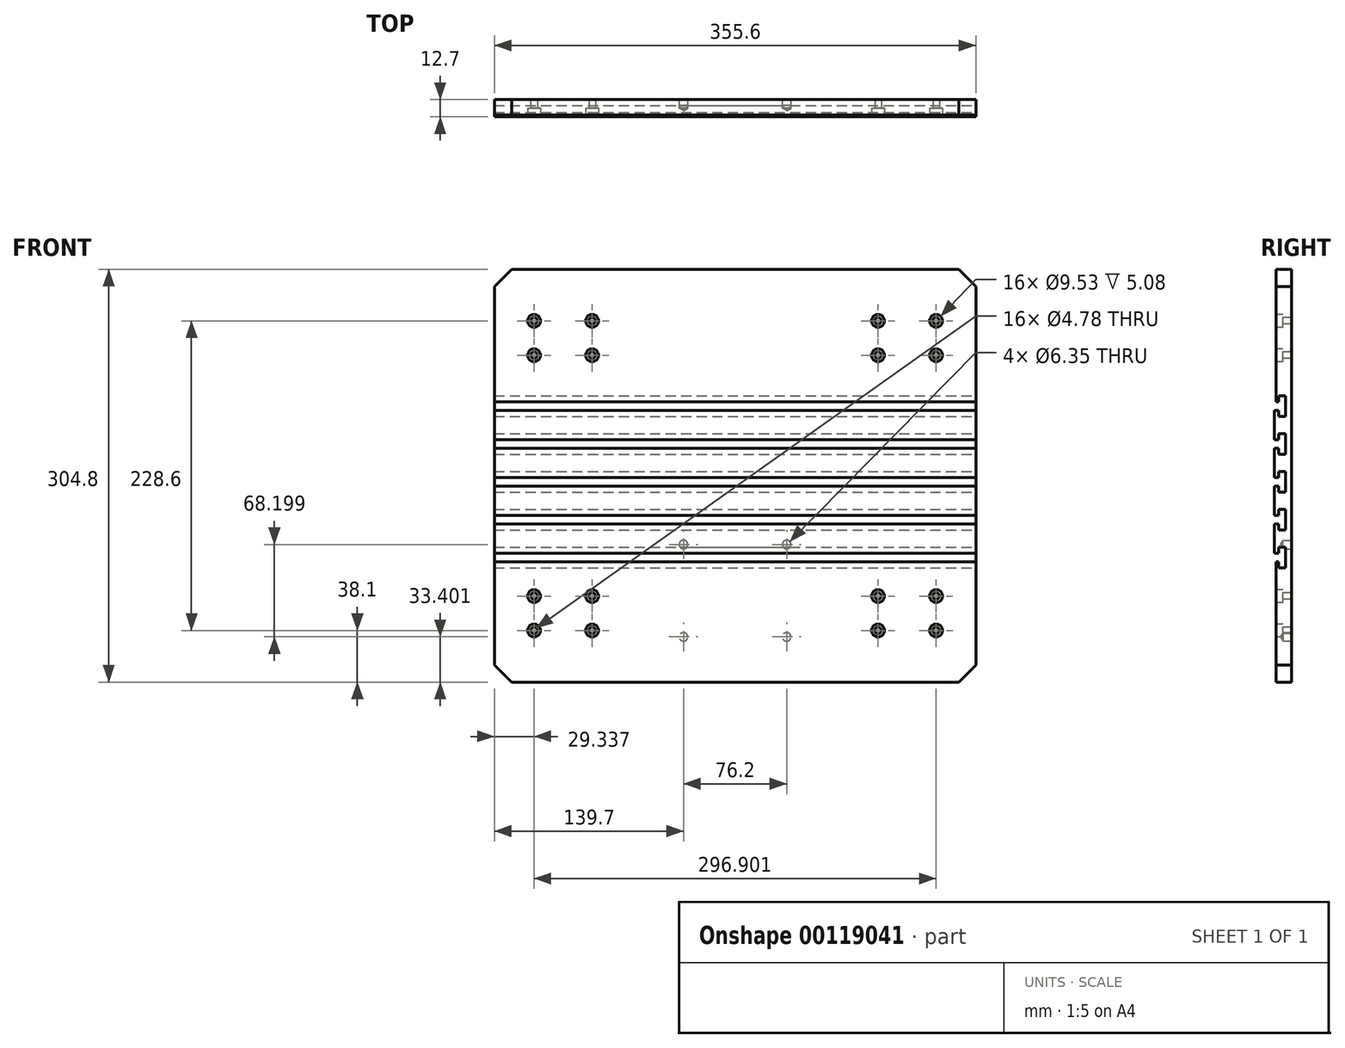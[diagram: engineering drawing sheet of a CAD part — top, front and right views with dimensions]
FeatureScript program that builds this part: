
annotation { "Feature Type Name" : "Feature", "Feature Type Description" : "" }
export const myFeature = defineFeature(function(context is Context, id is Id, definition is map)
    precondition{}
    {
        {
            var Q0;
            Q0=qCreatedBy(makeId("Front.planeOp"),FACE);
            var sketch = newSketch(context, id + "F0", { "sketchPlane" : qUnion([Q0])});
            skLineSegment(sketch, "E0.bottom", {"start": v(0, 0) * mm, "end": v(355.6, 0) * mm});
            skLineSegment(sketch, "E0.top", {"start": v(0, 304.8) * mm, "end": v(355.6, 304.8) * mm});
            skLineSegment(sketch, "E0.left", {"start": v(0, 0) * mm, "end": v(0, 304.8) * mm});
            skLineSegment(sketch, "E0.right", {"start": v(355.6, 0) * mm, "end": v(355.6, 304.8) * mm});
            skSolve(sketch);
        }
        {
            var Q0;
            Q0 = qSketchRegion(id + "F0", true);
            extrude(context, id + "F1", {"entities" : qUnion([Q0]), "depth" : 12.7 * mm});
        }
        {
            var Q0;
            Q0=makeQuery(id+"F1.opExtrude","CAP_FACE",FACE,{"disambiguationData":[OSD([sQuery(id+"F0.wireOp",EDGE,"E0.bottom"),sQuery(id+"F0.wireOp",EDGE,"E0.top"),sQuery(id+"F0.wireOp",EDGE,"E0.left"),sQuery(id+"F0.wireOp",EDGE,"E0.right")])],"isStart":false});
            var sketch = newSketch(context, id + "F2", { "sketchPlane" : qUnion([Q0])});
            skLineSegment(sketch, "E1.bottom", {"start": v(72.21, 266.7) * mm, "end": v(283.36, 266.7) * mm, "construction": true});
            skLineSegment(sketch, "E1.top", {"start": v(72.21, 38.1) * mm, "end": v(283.36, 38.1) * mm, "construction": true});
            skLineSegment(sketch, "E1.left", {"start": v(72.21, 266.7) * mm, "end": v(72.21, 38.1) * mm, "construction": true});
            skLineSegment(sketch, "E1.right", {"start": v(283.36, 266.7) * mm, "end": v(283.36, 38.1) * mm, "construction": true});
            skPoint(sketch, "E2", {"position": v(72.21, 266.7) * mm});
            skPoint(sketch, "E3", {"position": v(29.34, 266.7) * mm});
            skPoint(sketch, "E4", {"position": v(283.36, 266.7) * mm});
            skPoint(sketch, "E5", {"position": v(326.24, 266.7) * mm});
            skPoint(sketch, "E6", {"position": v(72.21, 38.1) * mm});
            skPoint(sketch, "E7", {"position": v(29.34, 38.1) * mm});
            skPoint(sketch, "E8", {"position": v(283.36, 38.1) * mm});
            skPoint(sketch, "E9", {"position": v(326.24, 38.1) * mm});
            skPoint(sketch, "E10", {"position": v(29.34, 241.3) * mm});
            skPoint(sketch, "E11", {"position": v(72.21, 241.3) * mm});
            skPoint(sketch, "E12", {"position": v(283.36, 241.3) * mm});
            skPoint(sketch, "E13", {"position": v(326.24, 241.3) * mm});
            skPoint(sketch, "E14", {"position": v(283.36, 63.5) * mm});
            skPoint(sketch, "E15", {"position": v(326.24, 63.5) * mm});
            skPoint(sketch, "E16", {"position": v(72.21, 63.5) * mm});
            skPoint(sketch, "E17", {"position": v(29.34, 63.5) * mm});
            skSolve(sketch);
        }
        {
            var Q0;
            Q0=sQuery(id+"F2.wireOp",VERTEX,"E3");
            var Q1;
            Q1=sQuery(id+"F2.wireOp",VERTEX,"E10");
            var Q2;
            Q2=sQuery(id+"F2.wireOp",VERTEX,"E11");
            var Q3;
            Q3=sQuery(id+"F2.wireOp",VERTEX,"E2");
            var Q4;
            Q4=sQuery(id+"F2.wireOp",VERTEX,"E17");
            var Q5;
            Q5=sQuery(id+"F2.wireOp",VERTEX,"E7");
            var Q6;
            Q6=sQuery(id+"F2.wireOp",VERTEX,"E6");
            var Q7;
            Q7=sQuery(id+"F2.wireOp",VERTEX,"E16");
            var Q8;
            Q8=sQuery(id+"F2.wireOp",VERTEX,"E14");
            var Q9;
            Q9=sQuery(id+"F2.wireOp",VERTEX,"E8");
            var Q10;
            Q10=sQuery(id+"F2.wireOp",VERTEX,"E9");
            var Q11;
            Q11=sQuery(id+"F2.wireOp",VERTEX,"E15");
            var Q12;
            Q12=sQuery(id+"F2.wireOp",VERTEX,"E13");
            var Q13;
            Q13=sQuery(id+"F2.wireOp",VERTEX,"E12");
            var Q14;
            Q14=sQuery(id+"F2.wireOp",VERTEX,"E4");
            var Q15;
            Q15=sQuery(id+"F2.wireOp",VERTEX,"E5");
            var Q16;
            Q16=makeQuery(id+"F1.opExtrude","SWEPT_BODY",BODY,{"disambiguationData":[OSD([sQuery(id+"F0.wireOp",EDGE,"E0.bottom"),sQuery(id+"F0.wireOp",EDGE,"E0.top"),sQuery(id+"F0.wireOp",EDGE,"E0.left"),sQuery(id+"F0.wireOp",EDGE,"E0.right")])]});
            hole(context, id + "F3", {"style" : HoleStyle.C_BORE, "endStyle" : HoleEndStyle.THROUGH, "holeDiameter" : 4.78 * mm, "cBoreDiameter" : 9.52 * mm, "cBoreDepth" : 6.35 * mm, "locations" : qUnion([Q0, Q1, Q2, Q3, Q4, Q5, Q6, Q7, Q8, Q9, Q10, Q11, Q12, Q13, Q14, Q15]), "scope" : qUnion([Q16]), "isTappedThrough" : true});
        }
        {
            var Q0;
            Q0=makeQuery(id+"F1.opExtrude","SWEPT_FACE",FACE,{"disambiguationData":[OSD([sQuery(id+"F0.wireOp",EDGE,"E0.right")])]});
            var sketch = newSketch(context, id + "F4", { "sketchPlane" : qUnion([Q0])});
            skPoint(sketch, "E18", {"position": v(-12.7, 88.9) * mm});
            skLineSegment(sketch, "E19", {"start": v(-12.7, 88.9) * mm, "end": v(-9.52, 88.9) * mm});
            skLineSegment(sketch, "E20", {"start": v(-9.52, 88.9) * mm, "end": v(-9.52, 84.45) * mm});
            skLineSegment(sketch, "E21", {"start": v(-9.52, 84.45) * mm, "end": v(-4.44, 84.45) * mm});
            skLineSegment(sketch, "E22", {"start": v(-4.44, 84.45) * mm, "end": v(-4.44, 99.7) * mm});
            skLineSegment(sketch, "E23", {"start": v(-4.44, 99.7) * mm, "end": v(-9.53, 99.7) * mm});
            skLineSegment(sketch, "E24", {"start": v(-9.53, 99.7) * mm, "end": v(-9.53, 95.25) * mm});
            skLineSegment(sketch, "E25", {"start": v(-9.53, 95.25) * mm, "end": v(-12.7, 95.25) * mm});
            skPoint(sketch, "E26", {"position": v(-4.45, 112.4) * mm});
            skLineSegment(sketch, "E27", {"start": v(-4.45, 112.4) * mm, "end": v(-4.45, 127.64) * mm});
            skLineSegment(sketch, "E28", {"start": v(-4.45, 127.64) * mm, "end": v(-9.53, 127.64) * mm});
            skLineSegment(sketch, "E29", {"start": v(-9.53, 127.64) * mm, "end": v(-9.53, 123.19) * mm});
            skLineSegment(sketch, "E30", {"start": v(-9.53, 123.19) * mm, "end": v(-12.7, 123.19) * mm});
            skLineSegment(sketch, "E31", {"start": v(-9.53, 112.4) * mm, "end": v(-4.45, 112.4) * mm});
            skLineSegment(sketch, "E32", {"start": v(-9.53, 112.4) * mm, "end": v(-9.53, 116.84) * mm});
            skLineSegment(sketch, "E33", {"start": v(-12.7, 116.87) * mm, "end": v(-9.53, 116.84) * mm});
            skPoint(sketch, "E34", {"position": v(-4.45, 127.64) * mm});
            skPoint(sketch, "E35", {"position": v(-4.45, 140.33) * mm});
            skLineSegment(sketch, "E36", {"start": v(-4.45, 140.33) * mm, "end": v(-4.45, 155.57) * mm});
            skLineSegment(sketch, "E37", {"start": v(-4.45, 155.57) * mm, "end": v(-9.53, 155.57) * mm});
            skLineSegment(sketch, "E38", {"start": v(-9.53, 155.57) * mm, "end": v(-9.53, 151.13) * mm});
            skLineSegment(sketch, "E39", {"start": v(-9.53, 151.13) * mm, "end": v(-12.7, 151.13) * mm});
            skLineSegment(sketch, "E40", {"start": v(-4.45, 140.33) * mm, "end": v(-9.53, 140.33) * mm});
            skLineSegment(sketch, "E41", {"start": v(-9.53, 140.33) * mm, "end": v(-9.53, 144.78) * mm});
            skLineSegment(sketch, "E42", {"start": v(-9.53, 144.78) * mm, "end": v(-12.7, 144.78) * mm});
            skPoint(sketch, "E43", {"position": v(-4.45, 168.27) * mm});
            skLineSegment(sketch, "E44", {"start": v(-4.45, 168.27) * mm, "end": v(-4.45, 183.51) * mm});
            skLineSegment(sketch, "E45", {"start": v(-4.45, 183.51) * mm, "end": v(-9.53, 183.51) * mm});
            skLineSegment(sketch, "E46", {"start": v(-9.53, 183.51) * mm, "end": v(-9.53, 179.07) * mm});
            skLineSegment(sketch, "E47", {"start": v(-9.53, 179.07) * mm, "end": v(-12.7, 179.07) * mm});
            skLineSegment(sketch, "E48", {"start": v(-4.45, 168.27) * mm, "end": v(-9.53, 168.27) * mm});
            skLineSegment(sketch, "E49", {"start": v(-9.53, 168.27) * mm, "end": v(-9.53, 172.72) * mm});
            skLineSegment(sketch, "E50", {"start": v(-9.53, 172.72) * mm, "end": v(-12.7, 172.72) * mm});
            skPoint(sketch, "E51", {"position": v(-4.45, 196.21) * mm});
            skLineSegment(sketch, "E52", {"start": v(-4.45, 196.21) * mm, "end": v(-4.45, 211.45) * mm});
            skLineSegment(sketch, "E53", {"start": v(-4.45, 211.45) * mm, "end": v(-9.53, 211.45) * mm});
            skLineSegment(sketch, "E54", {"start": v(-9.53, 211.45) * mm, "end": v(-9.53, 207) * mm});
            skLineSegment(sketch, "E55", {"start": v(-9.53, 207) * mm, "end": v(-12.7, 207) * mm});
            skLineSegment(sketch, "E56", {"start": v(-4.45, 196.21) * mm, "end": v(-9.53, 196.21) * mm});
            skLineSegment(sketch, "E57", {"start": v(-9.53, 196.21) * mm, "end": v(-9.53, 200.66) * mm});
            skLineSegment(sketch, "E58", {"start": v(-9.53, 200.66) * mm, "end": v(-12.7, 200.66) * mm});
            skSolve(sketch);
        }
        {
            var Q0;
            Q0=makeQuery(id+"F4.imprint","IMPRINT",FACE,{"disambiguationData":[TD([[makeQuery(id+"F4.imprint","IMPRINT",EDGE,{"derivedFrom":sQuery(id+"F4.wireOp",EDGE,"E52")}),1.0]])]});
            var Q1;
            Q1=makeQuery(id+"F4.imprint","IMPRINT",FACE,{"disambiguationData":[TD([[makeQuery(id+"F4.imprint","IMPRINT",EDGE,{"derivedFrom":sQuery(id+"F4.wireOp",EDGE,"E44")}),1.0]])]});
            var Q2;
            Q2=makeQuery(id+"F4.imprint","IMPRINT",FACE,{"disambiguationData":[TD([[makeQuery(id+"F4.imprint","IMPRINT",EDGE,{"derivedFrom":sQuery(id+"F4.wireOp",EDGE,"E36")}),1.0]])]});
            var Q3;
            Q3=makeQuery(id+"F4.imprint","IMPRINT",FACE,{"disambiguationData":[TD([[makeQuery(id+"F4.imprint","IMPRINT",EDGE,{"derivedFrom":sQuery(id+"F4.wireOp",EDGE,"E27")}),1.0]])]});
            var Q4;
            {var subQ0=sQuery(id+"F4.wireOp",EDGE,"E19");Q4=makeQuery(id+"F4.imprint","IMPRINT",FACE,{"disambiguationData":[TD([[makeQuery(id+"F4.imprint","IMPRINT",EDGE,{"derivedFrom":subQ0}),1.0]])]});}
            extrude(context, id + "F5", {"entities" : qUnion([Q0, Q1, Q2, Q3, Q4]), "operationType" : NewBodyOperationType.REMOVE, "endBound" : BoundingType.THROUGH_ALL, "oppositeDirection" : true, "depth" : 25.4 * mm});
        }
        {
            var Q0;
            {var subQ0=sQuery(id+"F0.wireOp",EDGE,"E0.left");var subQ1=sQuery(id+"F0.wireOp",EDGE,"E0.top");var subQ2=sQuery(id+"F0.wireOp",EDGE,"E0.right");Q0=makeQuery(id+"F5.boolean.opBoolean","SPLIT",FACE,{"disambiguationData":[TD([makeQuery(id+"F1.opExtrude","SWEPT_FACE",FACE,{"disambiguationData":[OSD([subQ1])]})])],"derivedFrom":makeQuery(id+"F1.opExtrude","CAP_FACE",FACE,{"disambiguationData":[OSD([sQuery(id+"F0.wireOp",EDGE,"E0.bottom"),subQ1,subQ0,subQ2])],"isStart":false})});}
            var sketch = newSketch(context, id + "F6", { "sketchPlane" : qUnion([Q0])});
            skPoint(sketch, "E59", {"position": v(114.3, 279.4) * mm});
            skPoint(sketch, "E60", {"position": v(114.3, 247.65) * mm});
            skPoint(sketch, "E61", {"position": v(241.3, 279.4) * mm});
            skPoint(sketch, "E62", {"position": v(241.3, 247.65) * mm});
            skLineSegment(sketch, "E63", {"start": v(114.3, 279.4) * mm, "end": v(241.3, 279.4) * mm, "construction": true});
            skLineSegment(sketch, "E64", {"start": v(241.3, 247.65) * mm, "end": v(241.3, 279.4) * mm, "construction": true});
            skLineSegment(sketch, "E65", {"start": v(241.3, 247.65) * mm, "end": v(114.3, 247.65) * mm, "construction": true});
            skLineSegment(sketch, "E66", {"start": v(114.3, 279.4) * mm, "end": v(114.3, 247.65) * mm, "construction": true});
            skLineSegment(sketch, "E67", {"start": v(177.8, 279.4) * mm, "end": v(177.8, 247.65) * mm, "construction": true});
            skSolve(sketch);
        }
        {
            var Q0;
            Q0 = qSketchRegion(id + "F6", true);
            var Q1;
            {var subQ2=sQuery(id+"F0.wireOp",EDGE,"E0.top");Q1=makeQuery(id+"F6.imprint","IMPRINT",FACE,{"disambiguationData":[TD([[makeQuery(id+"F6.imprint","IMPRINT",EDGE,{"derivedFrom":makeQuery(id+"F1.opExtrude","CAP_EDGE",EDGE,{"disambiguationData":[OSD([subQ2])],"isStart":false})}),-1.0]])]});}
            extrude(context, id + "F7", {"entities" : qUnion([Q0, Q1]), "operationType" : NewBodyOperationType.REMOVE, "oppositeDirection" : true, "depth" : 1.27 * mm});
        }
        {
            var Q0;
            {var subQ0=sQuery(id+"F0.wireOp",EDGE,"E0.bottom");var subQ1=sQuery(id+"F0.wireOp",EDGE,"E0.left");var subQ2=sQuery(id+"F0.wireOp",EDGE,"E0.right");Q0=makeQuery(id+"F5.boolean.opBoolean","SPLIT",FACE,{"disambiguationData":[TD([makeQuery(id+"F1.opExtrude","SWEPT_FACE",FACE,{"disambiguationData":[OSD([subQ0])]})])],"derivedFrom":makeQuery(id+"F1.opExtrude","CAP_FACE",FACE,{"disambiguationData":[OSD([subQ0,sQuery(id+"F0.wireOp",EDGE,"E0.top"),subQ1,subQ2])],"isStart":false})});}
            var sketch = newSketch(context, id + "F8", { "sketchPlane" : qUnion([Q0])});
            skPoint(sketch, "E68", {"position": v(127, 25.4) * mm});
            skPoint(sketch, "E69", {"position": v(127, 57.15) * mm});
            skPoint(sketch, "E70", {"position": v(228.6, 57.15) * mm});
            skPoint(sketch, "E71", {"position": v(228.6, 25.4) * mm});
            skLineSegment(sketch, "E72", {"start": v(127, 57.15) * mm, "end": v(127, 25.4) * mm, "construction": true});
            skLineSegment(sketch, "E73", {"start": v(228.6, 25.4) * mm, "end": v(127, 25.4) * mm, "construction": true});
            skLineSegment(sketch, "E74", {"start": v(127, 57.15) * mm, "end": v(228.6, 57.15) * mm, "construction": true});
            skLineSegment(sketch, "E75", {"start": v(228.6, 25.4) * mm, "end": v(228.6, 57.15) * mm, "construction": true});
            skLineSegment(sketch, "E76", {"start": v(177.8, 57.15) * mm, "end": v(177.8, 25.4) * mm, "construction": true});
            skSolve(sketch);
        }
        {
            var Q0;
            Q0 = qSketchRegion(id + "F8", true);
            var Q1;
            {var subQ0=sQuery(id+"F0.wireOp",EDGE,"E0.bottom");Q1=makeQuery(id+"F8.imprint","IMPRINT",FACE,{"disambiguationData":[TD([[makeQuery(id+"F8.imprint","IMPRINT",EDGE,{"derivedFrom":makeQuery(id+"F1.opExtrude","CAP_EDGE",EDGE,{"disambiguationData":[OSD([subQ0])],"isStart":false})}),1.0]])]});}
            extrude(context, id + "F9", {"entities" : qUnion([Q0, Q1]), "operationType" : NewBodyOperationType.REMOVE, "oppositeDirection" : true, "depth" : 1.27 * mm});
        }
        {
            var Q0;
            Q0=makeQuery(id+"F1.opExtrude","CAP_FACE",FACE,{"disambiguationData":[OSD([sQuery(id+"F0.wireOp",EDGE,"E0.bottom"),sQuery(id+"F0.wireOp",EDGE,"E0.top"),sQuery(id+"F0.wireOp",EDGE,"E0.left"),sQuery(id+"F0.wireOp",EDGE,"E0.right")])],"isStart":true});
            var sketch = newSketch(context, id + "F10", { "sketchPlane" : qUnion([Q0])});
            skPoint(sketch, "E77", {"position": v(-215.9, 101.6) * mm});
            skPoint(sketch, "E78", {"position": v(-215.9, 33.4) * mm});
            skPoint(sketch, "E79", {"position": v(-139.7, 101.6) * mm});
            skPoint(sketch, "E80", {"position": v(-139.7, 33.4) * mm});
            skSolve(sketch);
        }
        {
            var Q0;
            Q0=sQuery(id+"F10.wireOp",VERTEX,"E77");
            var Q1;
            Q1=sQuery(id+"F10.wireOp",VERTEX,"E78");
            var Q2;
            Q2=sQuery(id+"F10.wireOp",VERTEX,"E80");
            var Q3;
            Q3=sQuery(id+"F10.wireOp",VERTEX,"E79");
            var Q4;
            Q4=makeQuery(id+"F1.opExtrude","SWEPT_BODY",BODY,{"disambiguationData":[OSD([sQuery(id+"F0.wireOp",EDGE,"E0.bottom"),sQuery(id+"F0.wireOp",EDGE,"E0.top"),sQuery(id+"F0.wireOp",EDGE,"E0.left"),sQuery(id+"F0.wireOp",EDGE,"E0.right")])]});
            hole(context, id + "F11", {"style" : HoleStyle.SIMPLE, "endStyle" : HoleEndStyle.BLIND, "holeDiameter" : 6.35 * mm, "holeDepth" : 6.35 * mm, "locations" : qUnion([Q0, Q1, Q2, Q3]), "scope" : qUnion([Q4])});
        }
        {
            var Q0;
            Q0=makeQuery(id+"F1.opExtrude","SWEPT_EDGE",EDGE,{"disambiguationData":[OSD([sQuery(id+"F0.wireOp",EDGE,"E0.top"),sQuery(id+"F0.wireOp",EDGE,"E0.right")])]});
            var Q1;
            Q1=makeQuery(id+"F1.opExtrude","SWEPT_EDGE",EDGE,{"disambiguationData":[OSD([sQuery(id+"F0.wireOp",EDGE,"E0.bottom"),sQuery(id+"F0.wireOp",EDGE,"E0.right")])]});
            var Q2;
            Q2=makeQuery(id+"F1.opExtrude","SWEPT_EDGE",EDGE,{"disambiguationData":[OSD([sQuery(id+"F0.wireOp",EDGE,"E0.top"),sQuery(id+"F0.wireOp",EDGE,"E0.left")])]});
            var Q3;
            Q3=makeQuery(id+"F1.opExtrude","SWEPT_EDGE",EDGE,{"disambiguationData":[OSD([sQuery(id+"F0.wireOp",EDGE,"E0.bottom"),sQuery(id+"F0.wireOp",EDGE,"E0.left")])]});
            chamfer(context, id + "F12", {"entities" : qUnion([Q0, Q1, Q2, Q3]), "width" : 12.7 * mm, "tangentPropagation" : true});
        }
    });
